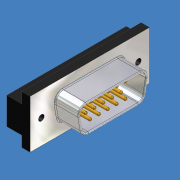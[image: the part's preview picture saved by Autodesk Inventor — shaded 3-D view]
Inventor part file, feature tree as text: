
AUTODESK INVENTOR PART (.ipt)
format: ipt  version: 2011 (Build 150239000, 239)  size: 222,720 bytes
history: native  units: mm (DEFAULTED — no unit token found)
features: sketch x4, extrude x3, fillet x2, hole x1, pattern_linear x1
ambient origin geometry x8: Origin, YZ Plane, XZ Plane, XY Plane, X Axis, Y Axis, Z Axis, Center Point
bodies: Solid1 (feature_tree)
feature tree (11):
  extrude  "Extrusion1"  Depth=2.16mm
  extrude  "Extrusion2"  Depth=12.5mm
  fillet  "Fillet1"  Radius=30.8mm
  hole  "Hole1"  [1 undecoded]
  extrude  "Extrusion3"  Depth=16.92mm
  fillet  "Fillet2"  Radius=0.5mm
  pattern_linear  "Rectangular Pattern1"  Spacing1=6.1mm  [1 undecoded]
  sketch  "Sketch1"  dims[d2=7.0mm d3=2.16mm]
  sketch  "Sketch2"  dims[d4=6.0mm d5=12.5mm d6=30.8mm d7=0.0mm]
  sketch  "Sketch3"  dims[d8=6.3mm d9=17.453293mm]
  sketch  "Sketch4"  dims[d11=1.5mm d12=16.92mm d13=0.5mm d14=6.1mm d15=0.0mm d16=0.25mm d17=25.0mm d18=1.5mm d19=6.0mm d20=4.0mm d21=2.0mm d22=14.3117mm d23=8.0mm d24=20.594885mm d27=1.98mm d28=4.56mm d29=5.0mm d30=0.0mm d31=0.76mm d32=0.38mm d33=100.0mm d35=1.14mm d36=30.0mm d38=1.98mm]
note: 2 required parameter values undecoded (feature->parameter linkage not recoverable at this tier; creation-order binding heuristic only, values carry confidence <= 0.55)
